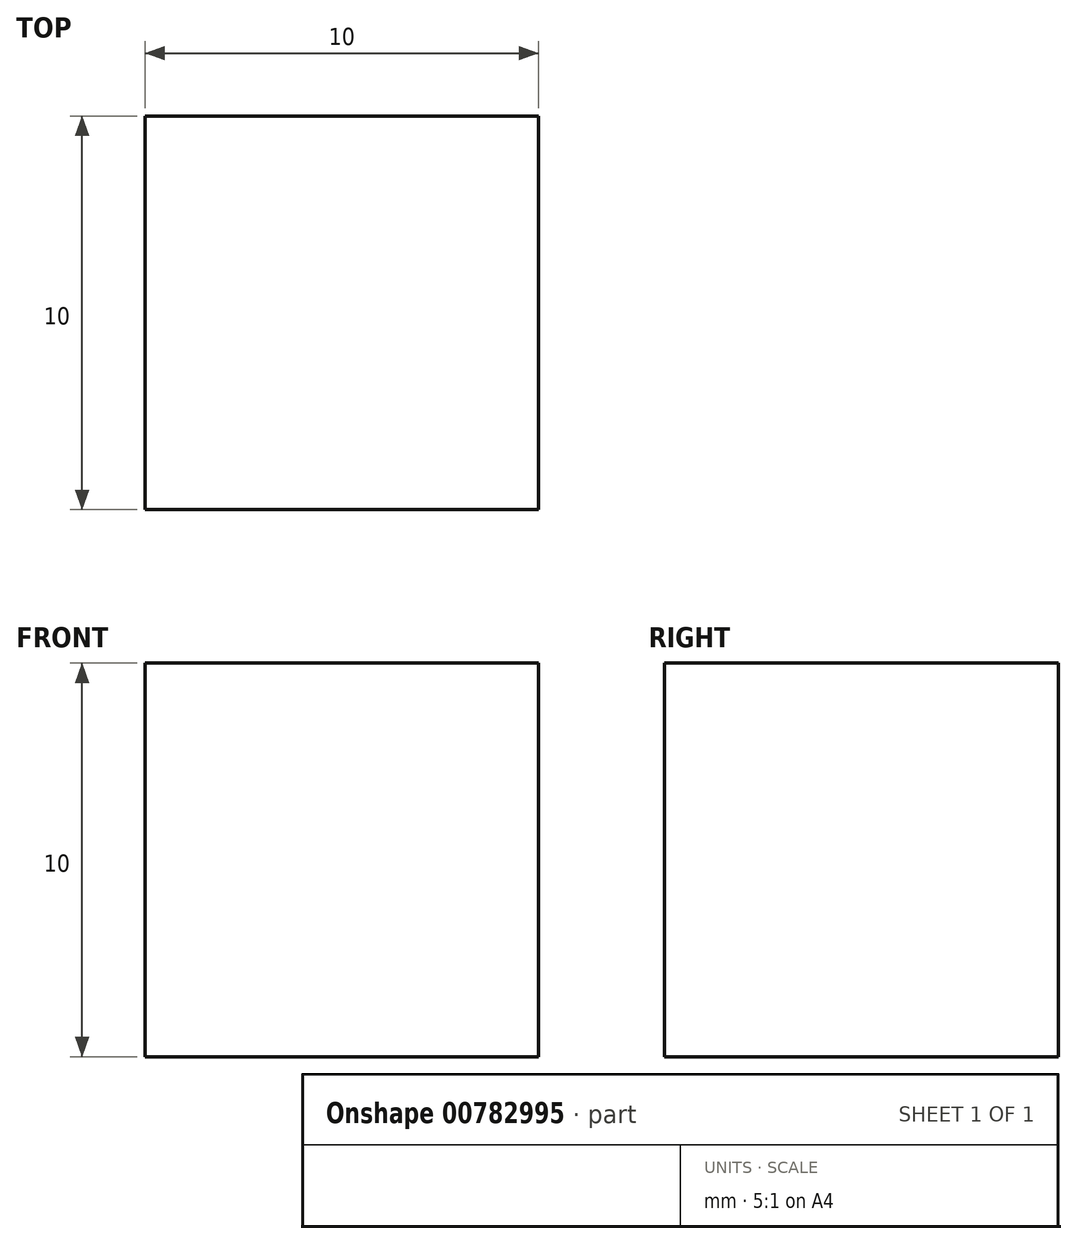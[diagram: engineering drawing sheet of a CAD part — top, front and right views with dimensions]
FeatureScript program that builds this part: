
annotation { "Feature Type Name" : "Feature", "Feature Type Description" : "" }
export const myFeature = defineFeature(function(context is Context, id is Id, definition is map)
    precondition{}
    {
        {
            var Q0;
            Q0=qCreatedBy(makeId("Top.planeOp"),FACE);
            var sketch = newSketch(context, id + "F0", { "sketchPlane" : qUnion([Q0])});
            skLineSegment(sketch, "E0.bottom", {"start": v(0, 0) * mm, "end": v(10, 0) * mm});
            skLineSegment(sketch, "E0.top", {"start": v(0, -10) * mm, "end": v(10, -10) * mm});
            skLineSegment(sketch, "E0.left", {"start": v(0, 0) * mm, "end": v(0, -10) * mm});
            skLineSegment(sketch, "E0.right", {"start": v(10, 0) * mm, "end": v(10, -10) * mm});
            skSolve(sketch);
        }
        {
            var Q0;
            Q0 = qSketchRegion(id + "F0", true);
            extrude(context, id + "F1", {"entities" : qUnion([Q0]), "depth" : 10 * mm, "offsetDistance" : 25 * mm});
        }
    });
